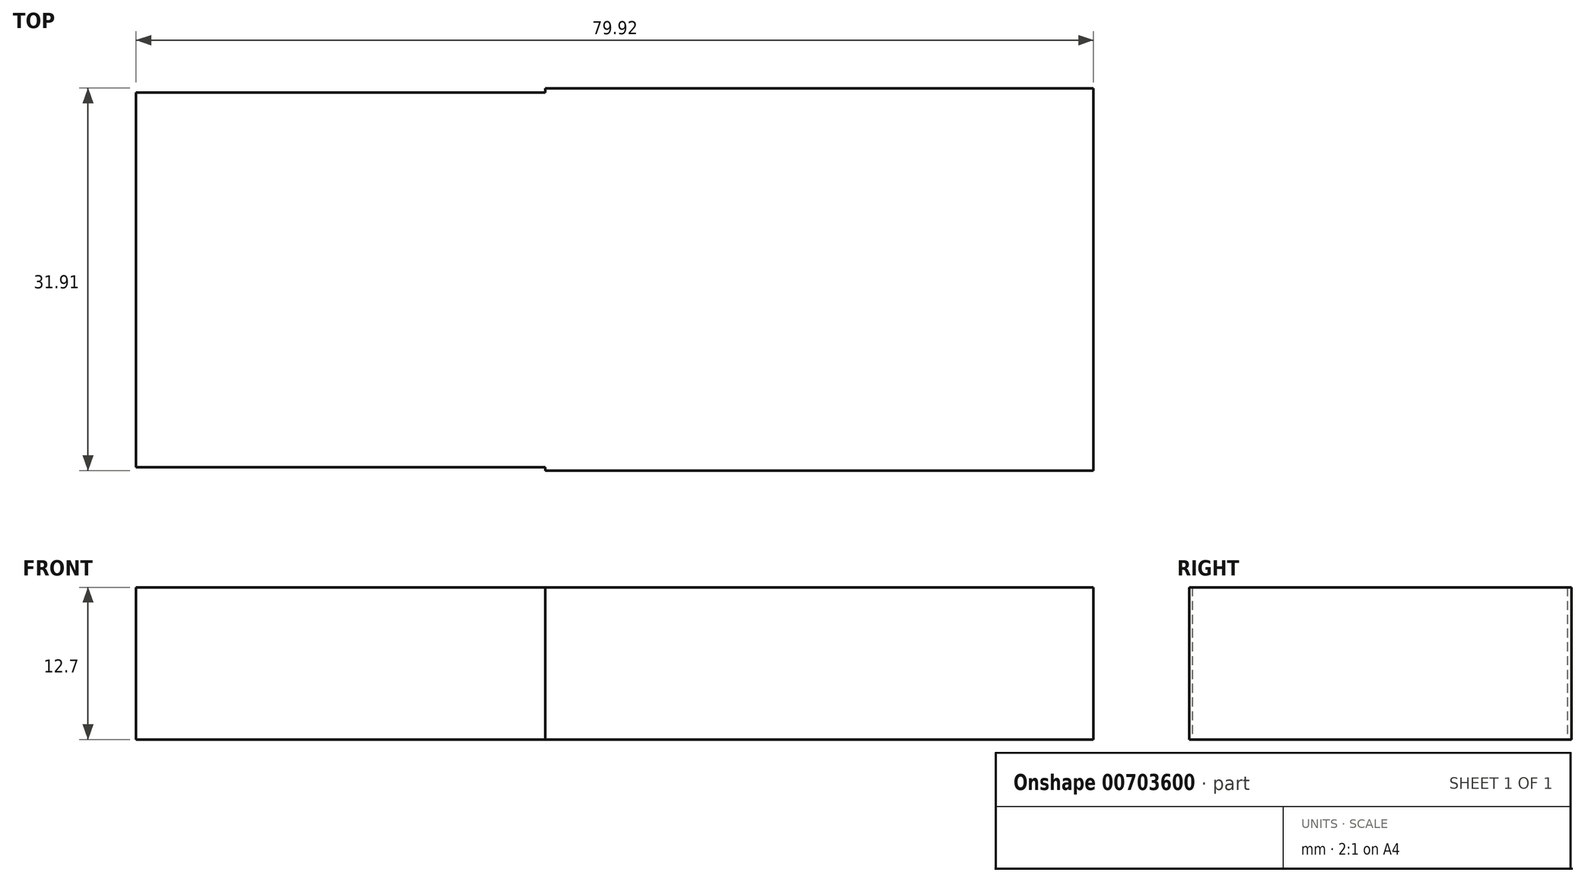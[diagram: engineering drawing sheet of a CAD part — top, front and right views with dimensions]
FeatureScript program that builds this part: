
annotation { "Feature Type Name" : "Feature", "Feature Type Description" : "" }
export const myFeature = defineFeature(function(context is Context, id is Id, definition is map)
    precondition{}
    {
        {
            var Q0;
            Q0=qCreatedBy(makeId("Top.planeOp"),FACE);
            var sketch = newSketch(context, id + "F0", { "sketchPlane" : qUnion([Q0])});
            skLineSegment(sketch, "E0.bottom", {"start": v(-69.52, 24.3) * mm, "end": v(-35.15, 24.3) * mm});
            skLineSegment(sketch, "E0.top", {"start": v(-69.52, -7) * mm, "end": v(-35.15, -7) * mm});
            skLineSegment(sketch, "E0.left", {"start": v(-69.52, 24.3) * mm, "end": v(-69.52, -7) * mm});
            skLineSegment(sketch, "E0.right", {"start": v(-35.15, 24.3) * mm, "end": v(-35.15, -7) * mm});
            skSolve(sketch);
        }
        {
            var Q0;
            Q0=makeQuery(id+"F0.imprint","IMPRINT",FACE,{"disambiguationData":[TD([[makeQuery(id+"F0.imprint","IMPRINT",EDGE,{"derivedFrom":sQuery(id+"F0.wireOp",EDGE,"E0.bottom")}),-1.0]])]});
            extrude(context, id + "F1", {"entities" : qUnion([Q0]), "depth" : 12.7 * mm, "offsetDistance" : 25.4 * mm});
        }
        {
            var Q0;
            Q0=qCreatedBy(makeId("Top.planeOp"),FACE);
            var sketch = newSketch(context, id + "F2", { "sketchPlane" : qUnion([Q0])});
            skLineSegment(sketch, "E1.bottom", {"start": v(-35.36, 24.66) * mm, "end": v(10.4, 24.66) * mm});
            skLineSegment(sketch, "E1.top", {"start": v(-35.36, -7.25) * mm, "end": v(10.4, -7.25) * mm});
            skLineSegment(sketch, "E1.left", {"start": v(-35.36, 24.66) * mm, "end": v(-35.36, -7.25) * mm});
            skLineSegment(sketch, "E1.right", {"start": v(10.4, 24.66) * mm, "end": v(10.4, -7.25) * mm});
            skSolve(sketch);
        }
        {
            var Q0;
            Q0=makeQuery(id+"F2.imprint","IMPRINT",FACE,{"disambiguationData":[TD([[makeQuery(id+"F2.imprint","IMPRINT",EDGE,{"derivedFrom":sQuery(id+"F2.wireOp",EDGE,"E1.bottom")}),-1.0]])]});
            extrude(context, id + "F3", {"entities" : qUnion([Q0]), "operationType" : NewBodyOperationType.ADD, "depth" : 12.7 * mm, "offsetDistance" : 25.4 * mm});
        }
    });
